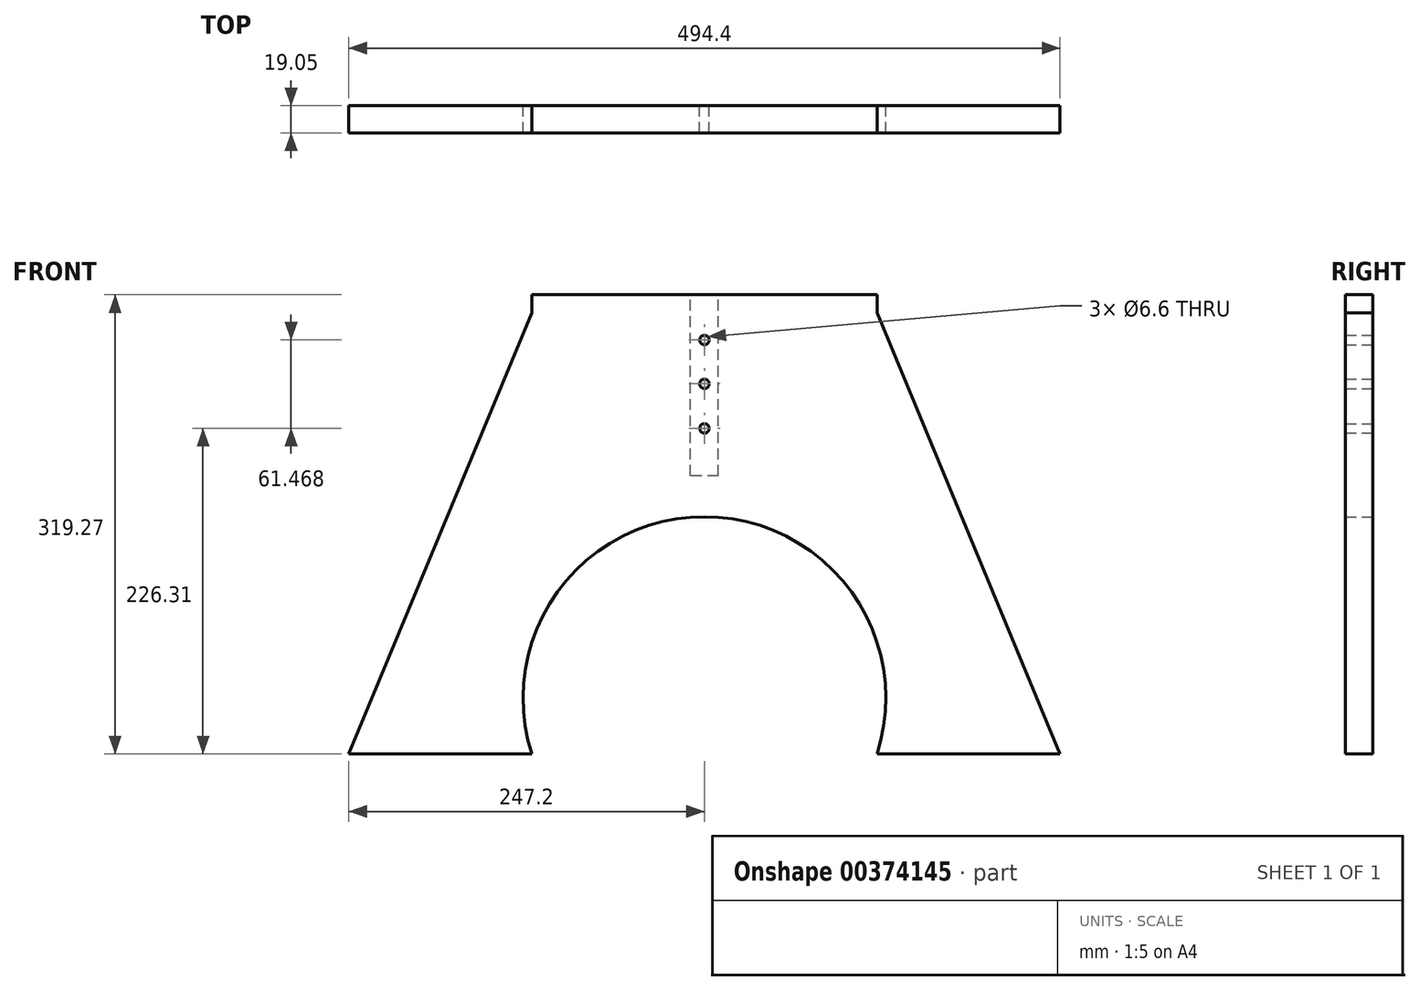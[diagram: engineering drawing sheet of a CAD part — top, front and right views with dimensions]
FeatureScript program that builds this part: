
annotation { "Feature Type Name" : "Feature", "Feature Type Description" : "" }
export const myFeature = defineFeature(function(context is Context, id is Id, definition is map)
    precondition{}
    {
        {
            var Q0;
            Q0=qCreatedBy(makeId("Front.planeOp"),FACE);
            var sketch = newSketch(context, id + "F0", { "sketchPlane" : qUnion([Q0])});
            skLineSegment(sketch, "E0", {"start": v(0, 155.77) * mm, "end": v(120.02, 155.77) * mm});
            skLineSegment(sketch, "E1", {"start": v(0, 155.77) * mm, "end": v(-120.02, 155.77) * mm});
            skLineSegment(sketch, "E2", {"start": v(247.2, -163.5) * mm, "end": v(120.02, -163.5) * mm});
            skLineSegment(sketch, "E3", {"start": v(0, 155.77) * mm, "end": v(0, 7.25) * mm, "construction": true});
            skLineSegment(sketch, "E4.MirrorCS", {"start": v(-247.2, -163.5) * mm, "end": v(-120.01, -163.5) * mm});
            skPoint(sketch, "E5.third.point", {"position": v(-120.01, -77.29) * mm});
            skLineSegment(sketch, "E6.trimOffspring", {"start": v(0, -115.14) * mm, "end": v(0, -120.4) * mm, "construction": true});
            skLineSegment(sketch, "E7", {"start": v(120.02, 155.77) * mm, "end": v(120.02, 143.07) * mm});
            skLineSegment(sketch, "E8", {"start": v(120.01, 143.07) * mm, "end": v(247.2, -163.5) * mm});
            skLineSegment(sketch, "E9", {"start": v(-120.02, 155.77) * mm, "end": v(-120.02, 143.07) * mm});
            skLineSegment(sketch, "E10", {"start": v(-120.02, 143.07) * mm, "end": v(-247.2, -163.5) * mm});
            skArc(sketch, "E11", {"start": v(120.02, -163.5) * mm, "mid": v(0, 1.38) * mm, "end": v(-120.01, -163.5) * mm});
            skPoint(sketch, "E11.third.point", {"position": v(-18.57, 0) * mm});
            skSolve(sketch);
        }
        {
            var Q0;
            Q0=qSketchRegion(id+"F0",true);
            extrude(context, id + "F1", {"entities" : qUnion([Q0]), "depth" : 19.05 * mm});
        }
        {
            var Q0;
            Q0=qCreatedBy(makeId("Front.planeOp"),FACE);
            var sketch = newSketch(context, id + "F2", { "sketchPlane" : qUnion([Q0])});
            skLineSegment(sketch, "E12", {"start": v(0, 0) * mm, "end": v(0, 29.8) * mm, "construction": true});
            skLineSegment(sketch, "E13", {"start": v(0, 29.8) * mm, "end": v(-9.65, 29.8) * mm});
            skPoint(sketch, "E14.orphan", {"position": v(0, 62.81) * mm});
            skLineSegment(sketch, "E15", {"start": v(0, 29.8) * mm, "end": v(0, 157.41) * mm, "construction": true});
            skLineSegment(sketch, "E16.MirrorCS", {"start": v(0, 29.8) * mm, "end": v(9.65, 29.8) * mm});
            skLineSegment(sketch, "E17", {"start": v(9.65, 29.8) * mm, "end": v(9.65, 155.77) * mm});
            skLineSegment(sketch, "E18", {"start": v(9.65, 155.77) * mm, "end": v(0, 155.77) * mm});
            skLineSegment(sketch, "E19.MirrorCS", {"start": v(-9.65, 29.8) * mm, "end": v(-9.65, 155.77) * mm});
            skLineSegment(sketch, "E20.MirrorCS", {"start": v(-9.65, 155.77) * mm, "end": v(0, 155.77) * mm});
            skCircle(sketch, "E21", {"center": v(0, 124.28) * mm, "radius": 3.3 * mm});
            skCircle(sketch, "E22", {"center": v(0, 93.8) * mm, "radius": 3.3 * mm});
            skCircle(sketch, "E23", {"center": v(0, 62.81) * mm, "radius": 3.3 * mm});
            skLineSegment(sketch, "E24", {"start": v(-4.83, 155.77) * mm, "end": v(-4.83, 93.8) * mm, "construction": true});
            skSolve(sketch);
        }
        {
            var Q0;
            Q0=qSketchRegion(id+"F2",true);
            extrude(context, id + "F3", {"entities" : qUnion([Q0]), "operationType" : NewBodyOperationType.REMOVE, "depth" : 3 / 203.2 * mm});
        }
        {
            var Q0;
            Q0=makeQuery(id+"F3.boolean.opBoolean","SPLIT",FACE,{"disambiguationData":[TD([makeQuery(id+"F3.opExtrude","SWEPT_FACE",FACE,{"disambiguationData":[OSD([sQuery(id+"F2.wireOp",EDGE,"E21")])]})])],"derivedFrom":makeQuery(id+"F1.opExtrude","CAP_FACE",FACE,{"disambiguationData":[OSD([sQuery(id+"F0.wireOp",EDGE,"E0"),sQuery(id+"F0.wireOp",EDGE,"E1"),sQuery(id+"F0.wireOp",EDGE,"E2"),sQuery(id+"F0.wireOp",EDGE,"E4.MirrorCS"),sQuery(id+"F0.wireOp",EDGE,"E5"),sQuery(id+"F0.wireOp",EDGE,"E7"),sQuery(id+"F0.wireOp",EDGE,"E8"),sQuery(id+"F0.wireOp",EDGE,"E9"),sQuery(id+"F0.wireOp",EDGE,"E10")])],"isStart":true})});
            var Q1;
            Q1=sQuery(id+"F2.wireOp",EDGE,"E21");
            extrude(context, id + "F4", {"entities" : qUnion([Q0]), "operationType" : NewBodyOperationType.REMOVE, "surfaceEntities" : qUnion([Q1]), "oppositeDirection" : true, "depth" : 19.05 * mm});
        }
        {
            var Q0;
            Q0=makeQuery(id+"F3.boolean.opBoolean","SPLIT",FACE,{"disambiguationData":[TD([makeQuery(id+"F3.opExtrude","SWEPT_FACE",FACE,{"disambiguationData":[OSD([sQuery(id+"F2.wireOp",EDGE,"E22")])]})])],"derivedFrom":makeQuery(id+"F1.opExtrude","CAP_FACE",FACE,{"disambiguationData":[OSD([sQuery(id+"F0.wireOp",EDGE,"E0"),sQuery(id+"F0.wireOp",EDGE,"E1"),sQuery(id+"F0.wireOp",EDGE,"E2"),sQuery(id+"F0.wireOp",EDGE,"E4.MirrorCS"),sQuery(id+"F0.wireOp",EDGE,"E5"),sQuery(id+"F0.wireOp",EDGE,"E7"),sQuery(id+"F0.wireOp",EDGE,"E8"),sQuery(id+"F0.wireOp",EDGE,"E9"),sQuery(id+"F0.wireOp",EDGE,"E10")])],"isStart":true})});
            var Q1;
            Q1=sQuery(id+"F2.wireOp",EDGE,"E22");
            extrude(context, id + "F5", {"entities" : qUnion([Q0]), "operationType" : NewBodyOperationType.REMOVE, "surfaceEntities" : qUnion([Q1]), "oppositeDirection" : true, "depth" : 19.05 * mm});
        }
        {
            var Q0;
            Q0=makeQuery(id+"F3.boolean.opBoolean","SPLIT",FACE,{"disambiguationData":[TD([makeQuery(id+"F3.opExtrude","SWEPT_FACE",FACE,{"disambiguationData":[OSD([sQuery(id+"F2.wireOp",EDGE,"E23")])]})])],"derivedFrom":makeQuery(id+"F1.opExtrude","CAP_FACE",FACE,{"disambiguationData":[OSD([sQuery(id+"F0.wireOp",EDGE,"E0"),sQuery(id+"F0.wireOp",EDGE,"E1"),sQuery(id+"F0.wireOp",EDGE,"E2"),sQuery(id+"F0.wireOp",EDGE,"E4.MirrorCS"),sQuery(id+"F0.wireOp",EDGE,"E5"),sQuery(id+"F0.wireOp",EDGE,"E7"),sQuery(id+"F0.wireOp",EDGE,"E8"),sQuery(id+"F0.wireOp",EDGE,"E9"),sQuery(id+"F0.wireOp",EDGE,"E10")])],"isStart":true})});
            var Q1;
            Q1=sQuery(id+"F2.wireOp",EDGE,"E23");
            extrude(context, id + "F6", {"entities" : qUnion([Q0]), "operationType" : NewBodyOperationType.REMOVE, "surfaceEntities" : qUnion([Q1]), "oppositeDirection" : true, "depth" : 19.05 * mm});
        }
    });
